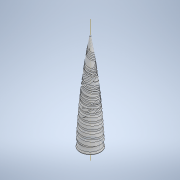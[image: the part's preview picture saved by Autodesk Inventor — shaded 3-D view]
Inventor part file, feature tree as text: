
AUTODESK INVENTOR PART (.ipt)
format: ipt  version: 2022 (Build 260153000, 153)  size: 2,014,720 bytes
history: native  units: in
note: dims shown in document units (in); Inventor stores cm internally (conversion verified against a paired STEP export)
features: sketch x7, helix x4, other x3, revolve x2, fillet x2, extrude x1
ambient origin geometry x8: Origin, YZ Plane, XZ Plane, XY Plane, X Axis, Y Axis, Z Axis, Center Point
bodies: Solid1 (feature_tree)
feature tree (19):
  other  "CrossSection1"
  extrude  "Extrusion1"  Depth=0.1969in
  revolve  "Revolution1"  Angle=360.0deg
  other  "Work Axis3"
  helix  "Coil3"  [1 undecoded]
  revolve  "Revolution2"  [1 undecoded]
  fillet  "Fillet2"  Radius=0.7677in
  other  "Work Axis7"
  helix  "Coil2"  [1 undecoded]
  fillet  "Fillet4"  Radius=0.1969in
  helix  "Coil4"  [1 undecoded]
  helix  "Coil5"  [1 undecoded]
  sketch  "Sketch1"  dims[d0=1.1811in d1=0.1969in]
  sketch  "Sketch2"  dims[d2=0.1181in d3=0.0in d7=360.0deg d8=0.4331in]
  sketch  "Sketch3"  dims[d19=0.4724in d20=0.2362in d21=0.7677in d22=360.0deg d24=0.1969in d26=0.1969in]
  sketch  "Sketch4"  dims[d29=1.5748in d30=0.3937in d31=1.378in d32=0.0447in d33=90.0deg d34=90.0deg d35=0.0in d36=0.0in d42=0.0787in]
  sketch  "Sketch5"  dims[d44=43.5197in]
  sketch  "Sketch6"  dims[d45=43.5039in]
  sketch  "Sketch7"  dims[d50=0.0in d54=0.3937in d55=0.3937in d56=5.5118in d57=-0.0275in d58=90.0deg d59=90.0deg d60=0.0in d61=0.0in d62=0.3937in d63=0.7677in d64=0.2362in d65=0.1575in d66=5.7087in d68=0.0394in d69=5.5118in d70=0.053in d71=0.0344in d72=0.0305in d73=0.1969in d74=0.2362in d75=0.1969in d77=0.0197in d78=0.0197in d79=0.2362in d80=0.2362in d81=0.2362in d82=0.2362in d83=0.1969in d84=0.0394in d86=0.0394in d87=0.2756in d88=0.2756in d89=0.2362in d90=0.7874in d91=0.3937in d92=3.937in d93=0.0412in d94=90.0deg d95=90.0deg d96=0.0in d97=0.0in d98=0.1181in d99=0.1181in d100=0.1181in d101=0.1575in d102=0.1575in d103=0.0236in d104=0.0236in d105=0.061in d107=0.7874in d108=0.3937in d109=3.937in d110=0.0481in d111=90.0deg d112=90.0deg d113=0.0in d114=0.0in d115=0.0197in d116=0.0787in d117=0.0in d118=0.7874in d119=0.3937in]
note: 5 required parameter values undecoded (feature->parameter linkage not recoverable at this tier; creation-order binding heuristic only, values carry confidence <= 0.55)